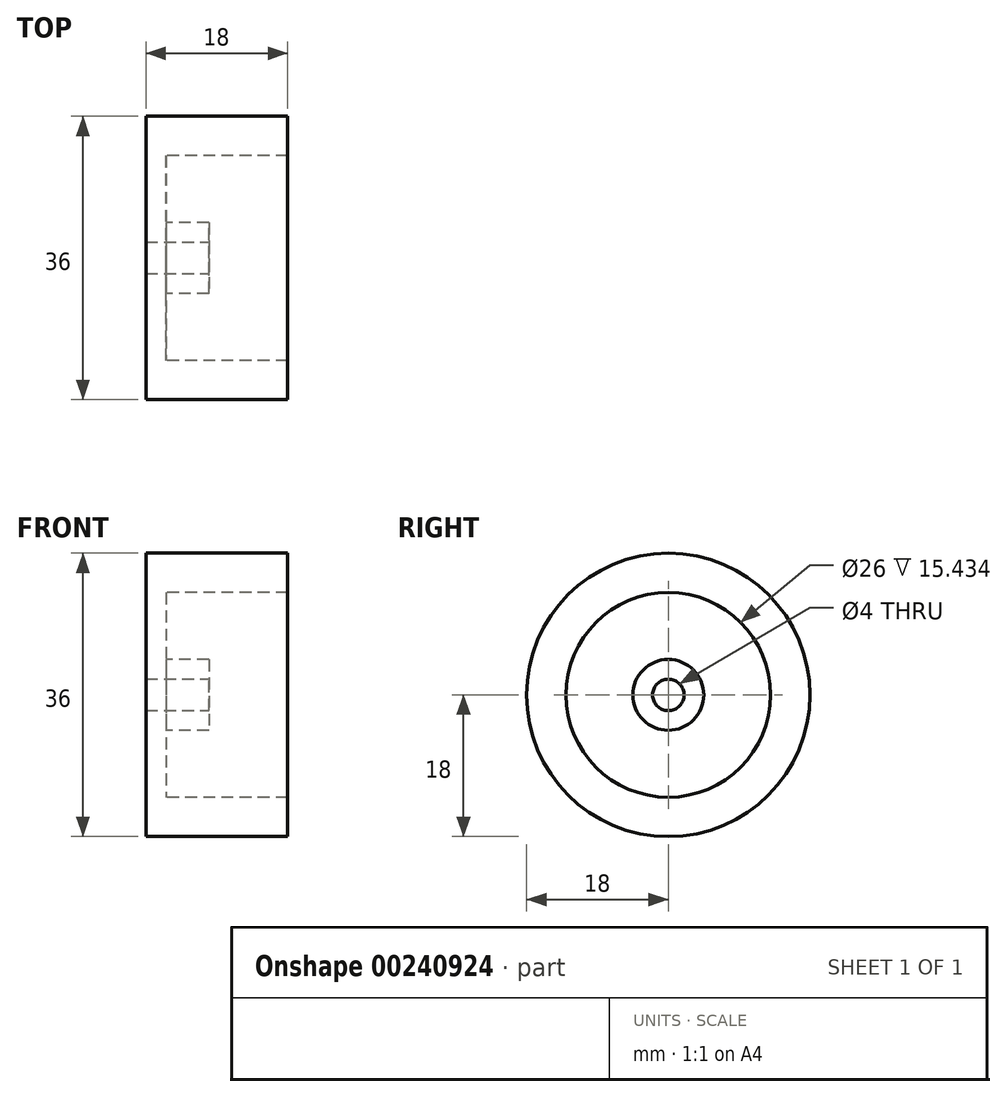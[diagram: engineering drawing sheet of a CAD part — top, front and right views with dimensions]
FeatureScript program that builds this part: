
annotation { "Feature Type Name" : "Feature", "Feature Type Description" : "" }
export const myFeature = defineFeature(function(context is Context, id is Id, definition is map)
    precondition{}
    {
        {
            var Q0;
            Q0=qCreatedBy(makeId("Front.planeOp"),FACE);
            var sketch = newSketch(context, id + "F0", { "sketchPlane" : qUnion([Q0])});
            skLineSegment(sketch, "E0", {"start": v(0, 0) * mm, "end": v(8, 0) * mm});
            skLineSegment(sketch, "E1", {"start": v(8, 0) * mm, "end": v(8, 4.5) * mm});
            skLineSegment(sketch, "E2", {"start": v(8, 4.5) * mm, "end": v(2.57, 4.5) * mm});
            skLineSegment(sketch, "E3", {"start": v(2.57, 4.5) * mm, "end": v(2.57, 13) * mm});
            skLineSegment(sketch, "E4", {"start": v(2.57, 13) * mm, "end": v(18, 13) * mm});
            skLineSegment(sketch, "E5", {"start": v(18, 13) * mm, "end": v(18, 18) * mm});
            skLineSegment(sketch, "E6", {"start": v(18, 18) * mm, "end": v(0, 18) * mm});
            skLineSegment(sketch, "E7", {"start": v(0, 18) * mm, "end": v(0, 0) * mm});
            skLineSegment(sketch, "E8", {"start": v(-75.8, 0) * mm, "end": v(79.5, 0) * mm, "construction": true});
            skSolve(sketch);
        }
        {
            var Q0;
            Q0 = qSketchRegion(id + "F0", true);
            var Q1;
            Q1=sQuery(id+"F0.wireOp",EDGE,"E8");
            revolve(context, id + "F1", {"entities" : qUnion([Q0]), "axis" : qUnion([Q1]), "revolveType" : RevolveType.FULL});
        }
        {
            var Q0;
            Q0=makeQuery(id+"F1.opRevolve","SWEPT_FACE",FACE,{"disambiguationData":[OSD([sQuery(id+"F0.wireOp",EDGE,"E1")])]});
            var sketch = newSketch(context, id + "F2", { "sketchPlane" : qUnion([Q0])});
            skCircle(sketch, "E9", {"center": v(0, 0) * mm, "radius": 2 * mm});
            skSolve(sketch);
        }
        {
            var Q0;
            Q0=makeQuery(id+"F2.imprint","IMPRINT",FACE,{"disambiguationData":[TD([[makeQuery(id+"F2.imprint","IMPRINT",EDGE,{"derivedFrom":sQuery(id+"F2.wireOp",EDGE,"E9")}),1.0]])]});
            extrude(context, id + "F3", {"entities" : qUnion([Q0]), "operationType" : NewBodyOperationType.REMOVE, "oppositeDirection" : true, "depth" : 25 * mm});
        }
    });
